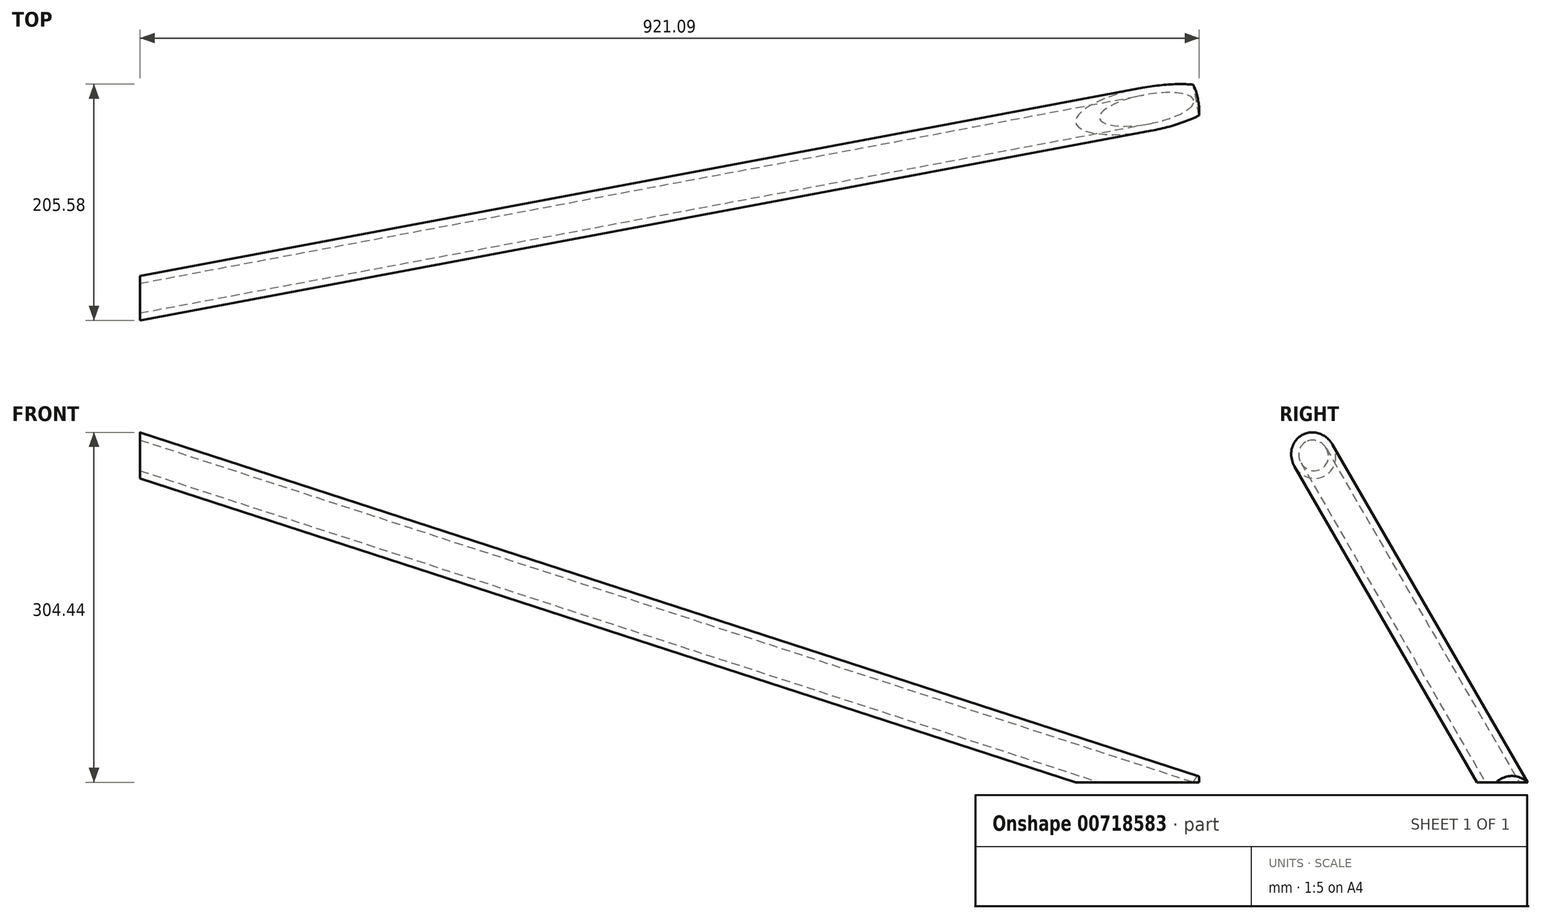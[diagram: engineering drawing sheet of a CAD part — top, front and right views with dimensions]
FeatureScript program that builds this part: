
annotation { "Feature Type Name" : "Feature", "Feature Type Description" : "" }
export const myFeature = defineFeature(function(context is Context, id is Id, definition is map)
    precondition{}
    {
        {
            var Q0;
            Q0=qCreatedBy(makeId("Front.planeOp"),FACE);
            var sketch = newSketch(context, id + "F0", { "sketchPlane" : qUnion([Q0])});
            skLineSegment(sketch, "E0", {"start": v(0, 0) * mm, "end": v(25.61, 78.82) * mm});
            skLineSegment(sketch, "E1", {"start": v(0, 0) * mm, "end": v(-36.28, 62.85) * mm});
            skSolve(sketch);
        }
        {
            var Q0;
            Q0=qCreatedBy(makeId("Right.planeOp"),FACE);
            var sketch = newSketch(context, id + "F1", { "sketchPlane" : qUnion([Q0])});
            skLineSegment(sketch, "E2", {"start": v(0, 0) * mm, "end": v(0, 69.88) * mm});
            skLineSegment(sketch, "E3", {"start": v(0, 0) * mm, "end": v(-68.68, -39.65) * mm});
            skSolve(sketch);
        }
        {
            var Q0;
            Q0=sQuery(id+"F1.wireOp",VERTEX,"E2.start");
            var Q1;
            Q1=sQuery(id+"F0.wireOp",VERTEX,"E0.end");
            var Q2;
            Q2=sQuery(id+"F1.wireOp",VERTEX,"E3.end");
            cPlane(context, id + "F2", {"entities" : qUnion([Q0, Q1, Q2]), "cplaneType" : CPlaneType.THREE_POINT, "offset" : 25.4 * mm, "width" : 152.4 * mm, "height" : 152.4 * mm});
        }
        {
            var Q0;
            Q0=qCreatedBy(id+"F2.planeOp",FACE);
            var sketch = newSketch(context, id + "F3", { "sketchPlane" : qUnion([Q0])});
            skCircle(sketch, "E4", {"center": v(0, 0) * mm, "radius": 19.05 * mm});
            skCircle(sketch, "E5", {"center": v(0, 0) * mm, "radius": 12.7 * mm});
            skSolve(sketch);
        }
        {
            var Q0;
            Q0=makeQuery(id+"F3.imprint","IMPRINT",FACE,{"disambiguationData":[TD([[makeQuery(id+"F3.imprint","IMPRINT",EDGE,{"derivedFrom":sQuery(id+"F3.wireOp",EDGE,"E4")}),1.0]])]});
            extrude(context, id + "F4", {"entities" : qUnion([Q0]), "depth" : 990.6 * mm, "offsetDistance" : 25.4 * mm});
        }
        {
            var Q0;
            Q0=qCreatedBy(makeId("Top.planeOp"),FACE);
            cPlane(context, id + "F5", {"entities" : qUnion([Q0]), "cplaneType" : CPlaneType.OFFSET, "offset" : 12.7 * mm, "width" : 152.4 * mm, "height" : 152.4 * mm});
        }
        {
            var Q0;
            Q0=makeQuery(id+"F4.opExtrude","CAP_FACE",FACE,{"disambiguationData":[OSD([sQuery(id+"F3.wireOp",EDGE,"E4")])],"isStart":true});
            var Q1;
            Q1=qCreatedBy(id+"F5.planeOp",FACE);
            extrude(context, id + "F6", {"entities" : qUnion([Q0]), "operationType" : NewBodyOperationType.REMOVE, "endBound" : BoundingType.UP_TO_SURFACE, "oppositeDirection" : true, "depth" : 25.4 * mm, "endBoundEntityFace" : qUnion([Q1]), "offsetDistance" : 25.4 * mm});
        }
        {
            var Q0;
            Q0=qCreatedBy(makeId("Right.planeOp"),FACE);
            cPlane(context, id + "F7", {"entities" : qUnion([Q0]), "cplaneType" : CPlaneType.OFFSET, "offset" : 914.4 * mm, "oppositeDirection" : true, "width" : 152.4 * mm, "height" : 152.4 * mm});
        }
        {
            var Q0;
            Q0=makeQuery(id+"F4.opExtrude","CAP_FACE",FACE,{"disambiguationData":[OSD([sQuery(id+"F3.wireOp",EDGE,"E4"),sQuery(id+"F3.wireOp",EDGE,"E5")])],"isStart":false});
            var Q1;
            Q1=qCreatedBy(id+"F7.planeOp",FACE);
            extrude(context, id + "F8", {"entities" : qUnion([Q0]), "operationType" : NewBodyOperationType.ADD, "endBound" : BoundingType.UP_TO_SURFACE, "oppositeDirection" : true, "depth" : 25.4 * mm, "endBoundEntityFace" : qUnion([Q1]), "offsetDistance" : 25.4 * mm});
        }
        {
            var Q0;
            Q0=makeQuery(id+"F4.opExtrude","CAP_FACE",FACE,{"disambiguationData":[OSD([sQuery(id+"F3.wireOp",EDGE,"E4"),sQuery(id+"F3.wireOp",EDGE,"E5")])],"isStart":false});
            var Q1;
            Q1=qCreatedBy(id+"F7.planeOp",FACE);
            extrude(context, id + "F9", {"entities" : qUnion([Q0]), "operationType" : NewBodyOperationType.ADD, "endBound" : BoundingType.UP_TO_SURFACE, "oppositeDirection" : true, "depth" : 25.4 * mm, "endBoundEntityFace" : qUnion([Q1]), "offsetDistance" : 25.4 * mm});
        }
        {
            var Q0;
            Q0=makeQuery(id+"F4.opExtrude","CAP_FACE",FACE,{"disambiguationData":[OSD([sQuery(id+"F3.wireOp",EDGE,"E4"),sQuery(id+"F3.wireOp",EDGE,"E5")])],"isStart":false});
            var Q1;
            Q1=qCreatedBy(id+"F7.planeOp",FACE);
            extrude(context, id + "F10", {"entities" : qUnion([Q0]), "operationType" : NewBodyOperationType.REMOVE, "endBound" : BoundingType.UP_TO_SURFACE, "oppositeDirection" : true, "depth" : 25.4 * mm, "endBoundEntityFace" : qUnion([Q1]), "offsetDistance" : 25.4 * mm});
        }
    });
